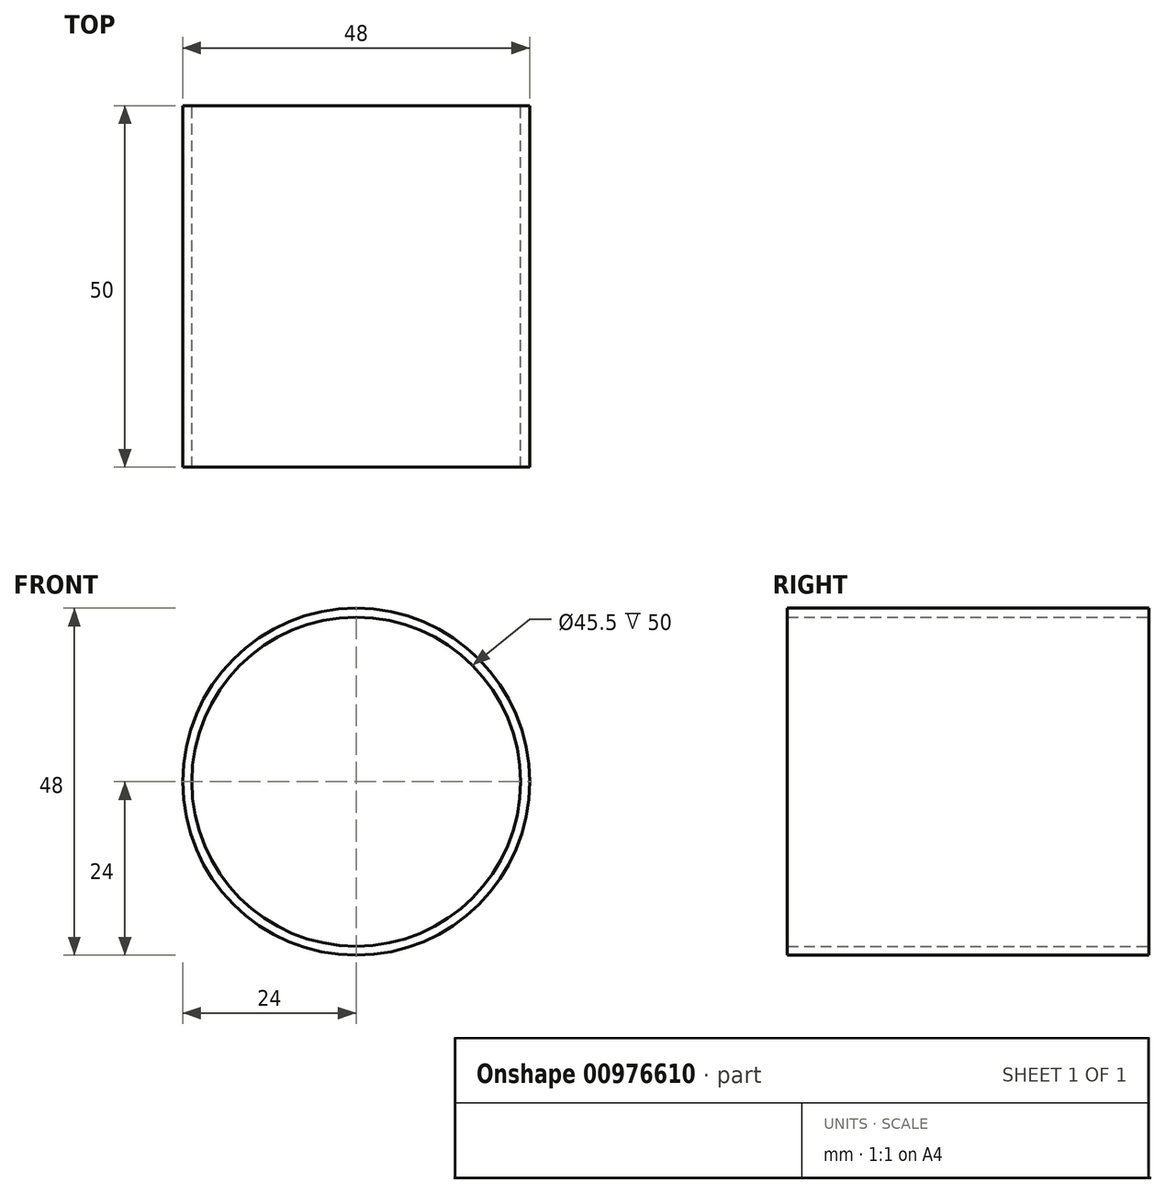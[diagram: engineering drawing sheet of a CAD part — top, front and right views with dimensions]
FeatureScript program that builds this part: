
annotation { "Feature Type Name" : "Feature", "Feature Type Description" : "" }
export const myFeature = defineFeature(function(context is Context, id is Id, definition is map)
    precondition{}
    {
        {
            var Q0;
            Q0=qCreatedBy(makeId("Front.planeOp"),FACE);
            var sketch = newSketch(context, id + "F0", { "sketchPlane" : qUnion([Q0])});
            skCircle(sketch, "E0", {"center": v(0, 0) * mm, "radius": 24 * mm});
            skCircle(sketch, "E1", {"center": v(0, 0) * mm, "radius": 22.75 * mm});
            skSolve(sketch);
        }
        {
            var Q0;
            Q0=makeQuery(id+"F0.imprint","IMPRINT",FACE,{"disambiguationData":[TD([[makeQuery(id+"F0.imprint","IMPRINT",EDGE,{"derivedFrom":sQuery(id+"F0.wireOp",EDGE,"E0")}),1.0]])]});
            extrude(context, id + "F1", {"entities" : qUnion([Q0]), "depth" : 50 * mm, "offsetDistance" : 25 * mm});
        }
    });
